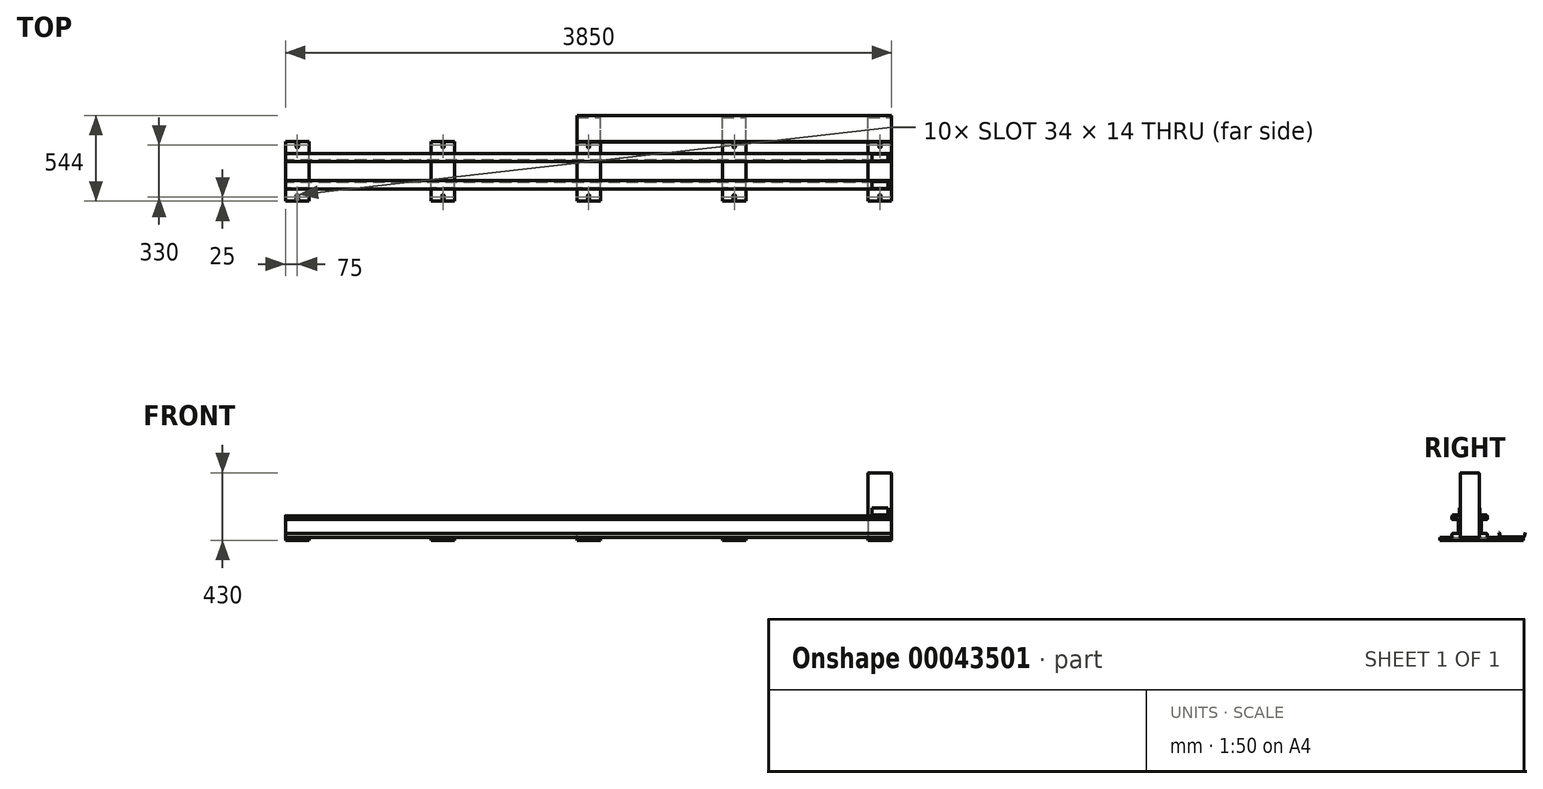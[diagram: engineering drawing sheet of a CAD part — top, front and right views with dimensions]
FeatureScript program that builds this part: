
annotation { "Feature Type Name" : "Feature", "Feature Type Description" : "" }
export const myFeature = defineFeature(function(context is Context, id is Id, definition is map)
    precondition{}
    {
        {
            var Q0;
            Q0=qCreatedBy(makeId("Top.planeOp"),FACE);
            var sketch = newSketch(context, id + "F0", { "sketchPlane" : qUnion([Q0])});
            skLineSegment(sketch, "E0.rect.bottom", {"start": v(-1925, 190) * mm, "end": v(1925, 190) * mm, "construction": true});
            skLineSegment(sketch, "E0.rect.top", {"start": v(-1925, -190) * mm, "end": v(1925, -190) * mm, "construction": true});
            skLineSegment(sketch, "E0.rect.left", {"start": v(-1925, 190) * mm, "end": v(-1925, -190) * mm, "construction": true});
            skLineSegment(sketch, "E0.rect.right", {"start": v(1925, 190) * mm, "end": v(1925, -190) * mm, "construction": true});
            skPoint(sketch, "E0.rect.middle", {"position": v(0, 0) * mm});
            skLineSegment(sketch, "E1.bottom", {"start": v(-1925, -190) * mm, "end": v(-1775, -190) * mm});
            skLineSegment(sketch, "E1.top", {"start": v(-1925, 190) * mm, "end": v(-1775, 190) * mm});
            skLineSegment(sketch, "E1.left", {"start": v(-1925, -190) * mm, "end": v(-1925, 190) * mm});
            skLineSegment(sketch, "E1.right", {"start": v(-1775, -190) * mm, "end": v(-1775, 190) * mm});
            skLineSegment(sketch, "E2", {"start": v(-1607.82, 0) * mm, "end": v(-2050.24, 0) * mm, "construction": true});
            skPoint(sketch, "E2.startSnap0", {"position": v(-1775, 0) * mm});
            skPoint(sketch, "E2.endSnap0", {"position": v(-1775, 0) * mm});
            skLineSegment(sketch, "E3", {"start": v(-1850, 190) * mm, "end": v(-1850, -266.2) * mm, "construction": true});
            skPoint(sketch, "E3.endSnap0", {"position": v(-1850, -190) * mm});
            skLineSegment(sketch, "E4.0", {"start": v(-1607.82, 155) * mm, "end": v(-2050.24, 155) * mm, "construction": true});
            skLineSegment(sketch, "E5.0", {"start": v(-1607.82, 175) * mm, "end": v(-2050.24, 175) * mm, "construction": true});
            skLineSegment(sketch, "E6", {"start": v(-1850, 175) * mm, "end": v(-1850, 155) * mm});
            skArc(sketch, "E7.0.startCap", {"start": v(-1857, 175) * mm, "mid": v(-1850, 182) * mm, "end": v(-1843, 175) * mm});
            skArc(sketch, "E7.0.endCap", {"start": v(-1843, 155) * mm, "mid": v(-1850, 148) * mm, "end": v(-1857, 155) * mm});
            skLineSegment(sketch, "E7.0.left", {"start": v(-1843, 175) * mm, "end": v(-1843, 155) * mm});
            skLineSegment(sketch, "E7.0.right", {"start": v(-1857, 175) * mm, "end": v(-1857, 155) * mm});
            skLineSegment(sketch, "E8.MirrorCS", {"start": v(-1857, -175) * mm, "end": v(-1857, -155) * mm});
            skLineSegment(sketch, "E9.MirrorCS", {"start": v(-1850, -175) * mm, "end": v(-1850, -155) * mm});
            skArc(sketch, "E10.MirrorCS", {"start": v(-1857, -175) * mm, "mid": v(-1850, -182) * mm, "end": v(-1843, -175) * mm});
            skArc(sketch, "E11.MirrorCS", {"start": v(-1843, -155) * mm, "mid": v(-1850, -148) * mm, "end": v(-1857, -155) * mm});
            skLineSegment(sketch, "E12.MirrorCS", {"start": v(-1843, -175) * mm, "end": v(-1843, -155) * mm});
            skLineSegment(sketch, "E13.1.0.0", {"start": v(-1000, -190) * mm, "end": v(-850, -190) * mm});
            skLineSegment(sketch, "E13.1.0.1", {"start": v(-1000, 190) * mm, "end": v(-850, 190) * mm});
            skPoint(sketch, "E13.1.0.2", {"position": v(-850, 0) * mm});
            skLineSegment(sketch, "E13.1.0.3", {"start": v(-1000, -190) * mm, "end": v(-1000, 190) * mm});
            skLineSegment(sketch, "E13.1.0.4", {"start": v(-850, -190) * mm, "end": v(-850, 190) * mm});
            skPoint(sketch, "E13.1.0.5", {"position": v(-925, -190) * mm});
            skLineSegment(sketch, "E13.1.0.6", {"start": v(-1000, 190) * mm, "end": v(-1000, -190) * mm, "construction": true});
            skPoint(sketch, "E13.1.0.7", {"position": v(-850, 0) * mm});
            skLineSegment(sketch, "E13.1.0.8", {"start": v(-932, -175) * mm, "end": v(-932, -155) * mm});
            skArc(sketch, "E13.1.0.9", {"start": v(-932, 175) * mm, "mid": v(-925, 182) * mm, "end": v(-918, 175) * mm});
            skArc(sketch, "E13.1.0.10", {"start": v(-932, -175) * mm, "mid": v(-925, -182) * mm, "end": v(-918, -175) * mm});
            skArc(sketch, "E13.1.0.11", {"start": v(-918, 155) * mm, "mid": v(-925, 148) * mm, "end": v(-932, 155) * mm});
            skLineSegment(sketch, "E13.1.0.12", {"start": v(-918, 175) * mm, "end": v(-918, 155) * mm});
            skLineSegment(sketch, "E13.1.0.13", {"start": v(-918, -175) * mm, "end": v(-918, -155) * mm});
            skLineSegment(sketch, "E13.1.0.14", {"start": v(-925, 175) * mm, "end": v(-925, 155) * mm});
            skLineSegment(sketch, "E13.1.0.15", {"start": v(-925, -175) * mm, "end": v(-925, -155) * mm});
            skLineSegment(sketch, "E13.1.0.16", {"start": v(-932, 175) * mm, "end": v(-932, 155) * mm});
            skArc(sketch, "E13.1.0.17", {"start": v(-918, -155) * mm, "mid": v(-925, -148) * mm, "end": v(-932, -155) * mm});
            skLineSegment(sketch, "E13.2.0.0", {"start": v(-75, -190) * mm, "end": v(75, -190) * mm});
            skPoint(sketch, "E13.2.0.2", {"position": v(75, 0) * mm});
            skLineSegment(sketch, "E13.2.0.3", {"start": v(-75, -190) * mm, "end": v(-75, 190) * mm});
            skLineSegment(sketch, "E13.2.0.4", {"start": v(75, -190) * mm, "end": v(75, 190) * mm});
            skPoint(sketch, "E13.2.0.5", {"position": v(0, -190) * mm});
            skLineSegment(sketch, "E13.2.0.6", {"start": v(-75, 190) * mm, "end": v(-75, -190) * mm, "construction": true});
            skPoint(sketch, "E13.2.0.7", {"position": v(75, 0) * mm});
            skLineSegment(sketch, "E13.2.0.8", {"start": v(-7, -175) * mm, "end": v(-7, -155) * mm});
            skArc(sketch, "E13.2.0.9", {"start": v(-7, 175) * mm, "mid": v(0, 182) * mm, "end": v(7, 175) * mm});
            skArc(sketch, "E13.2.0.10", {"start": v(-7, -175) * mm, "mid": v(0, -182) * mm, "end": v(7, -175) * mm});
            skArc(sketch, "E13.2.0.11", {"start": v(7, 155) * mm, "mid": v(0, 148) * mm, "end": v(-7, 155) * mm});
            skLineSegment(sketch, "E13.2.0.12", {"start": v(7, 175) * mm, "end": v(7, 155) * mm});
            skLineSegment(sketch, "E13.2.0.13", {"start": v(7, -175) * mm, "end": v(7, -155) * mm});
            skLineSegment(sketch, "E13.2.0.14", {"start": v(0, 175) * mm, "end": v(0, 155) * mm});
            skLineSegment(sketch, "E13.2.0.15", {"start": v(0, -175) * mm, "end": v(0, -155) * mm});
            skLineSegment(sketch, "E13.2.0.16", {"start": v(-7, 175) * mm, "end": v(-7, 155) * mm});
            skArc(sketch, "E13.2.0.17", {"start": v(7, -155) * mm, "mid": v(0, -148) * mm, "end": v(-7, -155) * mm});
            skLineSegment(sketch, "E13.3.0.0", {"start": v(850, -190) * mm, "end": v(1000, -190) * mm});
            skPoint(sketch, "E13.3.0.2", {"position": v(1000, 0) * mm});
            skLineSegment(sketch, "E13.3.0.3", {"start": v(850, -190) * mm, "end": v(850, 190) * mm});
            skLineSegment(sketch, "E13.3.0.4", {"start": v(1000, -190) * mm, "end": v(1000, 190) * mm});
            skPoint(sketch, "E13.3.0.5", {"position": v(925, -190) * mm});
            skLineSegment(sketch, "E13.3.0.6", {"start": v(850, 190) * mm, "end": v(850, -190) * mm, "construction": true});
            skPoint(sketch, "E13.3.0.7", {"position": v(1000, 0) * mm});
            skLineSegment(sketch, "E13.3.0.8", {"start": v(918, -175) * mm, "end": v(918, -155) * mm});
            skArc(sketch, "E13.3.0.9", {"start": v(918, 175) * mm, "mid": v(925, 182) * mm, "end": v(932, 175) * mm});
            skArc(sketch, "E13.3.0.10", {"start": v(918, -175) * mm, "mid": v(925, -182) * mm, "end": v(932, -175) * mm});
            skArc(sketch, "E13.3.0.11", {"start": v(932, 155) * mm, "mid": v(925, 148) * mm, "end": v(918, 155) * mm});
            skLineSegment(sketch, "E13.3.0.12", {"start": v(932, 175) * mm, "end": v(932, 155) * mm});
            skLineSegment(sketch, "E13.3.0.13", {"start": v(932, -175) * mm, "end": v(932, -155) * mm});
            skLineSegment(sketch, "E13.3.0.14", {"start": v(925, 175) * mm, "end": v(925, 155) * mm});
            skLineSegment(sketch, "E13.3.0.15", {"start": v(925, -175) * mm, "end": v(925, -155) * mm});
            skLineSegment(sketch, "E13.3.0.16", {"start": v(918, 175) * mm, "end": v(918, 155) * mm});
            skArc(sketch, "E13.3.0.17", {"start": v(932, -155) * mm, "mid": v(925, -148) * mm, "end": v(918, -155) * mm});
            skLineSegment(sketch, "E13.4.0.0", {"start": v(1775, -190) * mm, "end": v(1925, -190) * mm});
            skPoint(sketch, "E13.4.0.2", {"position": v(1925, 0) * mm});
            skLineSegment(sketch, "E13.4.0.3", {"start": v(1775, -190) * mm, "end": v(1775, 190) * mm});
            skLineSegment(sketch, "E13.4.0.4", {"start": v(1925, -190) * mm, "end": v(1925, 190) * mm});
            skPoint(sketch, "E13.4.0.5", {"position": v(1850, -190) * mm});
            skLineSegment(sketch, "E13.4.0.6", {"start": v(1775, 190) * mm, "end": v(1775, -190) * mm, "construction": true});
            skPoint(sketch, "E13.4.0.7", {"position": v(1925, 0) * mm});
            skLineSegment(sketch, "E13.4.0.8", {"start": v(1843, -175) * mm, "end": v(1843, -155) * mm});
            skArc(sketch, "E13.4.0.9", {"start": v(1843, 175) * mm, "mid": v(1850, 182) * mm, "end": v(1857, 175) * mm});
            skArc(sketch, "E13.4.0.10", {"start": v(1843, -175) * mm, "mid": v(1850, -182) * mm, "end": v(1857, -175) * mm});
            skArc(sketch, "E13.4.0.11", {"start": v(1857, 155) * mm, "mid": v(1850, 148) * mm, "end": v(1843, 155) * mm});
            skLineSegment(sketch, "E13.4.0.12", {"start": v(1857, 175) * mm, "end": v(1857, 155) * mm});
            skLineSegment(sketch, "E13.4.0.13", {"start": v(1857, -175) * mm, "end": v(1857, -155) * mm});
            skLineSegment(sketch, "E13.4.0.14", {"start": v(1850, 175) * mm, "end": v(1850, 155) * mm});
            skLineSegment(sketch, "E13.4.0.15", {"start": v(1850, -175) * mm, "end": v(1850, -155) * mm});
            skLineSegment(sketch, "E13.4.0.16", {"start": v(1843, 175) * mm, "end": v(1843, 155) * mm});
            skArc(sketch, "E13.4.0.17", {"start": v(1857, -155) * mm, "mid": v(1850, -148) * mm, "end": v(1843, -155) * mm});
            skLineSegment(sketch, "E13.direction1", {"start": v(-1925, -190) * mm, "end": v(-1000, -190) * mm, "construction": true});
            skLineSegment(sketch, "E14.top", {"start": v(-75, 340) * mm, "end": v(75, 340) * mm});
            skLineSegment(sketch, "E14.left", {"start": v(-75, -190) * mm, "end": v(-75, 340) * mm});
            skLineSegment(sketch, "E14.right", {"start": v(75, -190) * mm, "end": v(75, 340) * mm});
            skLineSegment(sketch, "E15.1.0.0", {"start": v(850, 340) * mm, "end": v(1000, 340) * mm});
            skLineSegment(sketch, "E15.1.0.1", {"start": v(1000, -190) * mm, "end": v(1000, 340) * mm});
            skLineSegment(sketch, "E15.1.0.2", {"start": v(850, -190) * mm, "end": v(850, 340) * mm});
            skLineSegment(sketch, "E15.2.0.0", {"start": v(1775, 340) * mm, "end": v(1925, 340) * mm});
            skLineSegment(sketch, "E15.2.0.1", {"start": v(1925, -190) * mm, "end": v(1925, 340) * mm});
            skLineSegment(sketch, "E15.2.0.2", {"start": v(1775, -190) * mm, "end": v(1775, 340) * mm});
            skLineSegment(sketch, "E15.direction1", {"start": v(-75, 340) * mm, "end": v(850, 340) * mm, "construction": true});
            skSolve(sketch);
        }
        {
            var Q0;
            Q0=qSketchRegion(id+"F0",true);
            extrude(context, id + "F1", {"entities" : qUnion([Q0]), "oppositeDirection" : true, "depth" : 20 * mm});
        }
        {
            var Q0;
            Q0=qCreatedBy(makeId("Right.planeOp"),FACE);
            var sketch = newSketch(context, id + "F2", { "sketchPlane" : qUnion([Q0])});
            skLineSegment(sketch, "E16", {"start": v(0, 0) * mm, "end": v(0, 313.62) * mm, "construction": true});
            skLineSegment(sketch, "E17.0", {"start": v(-113, 0) * mm, "end": v(-113, 313.62) * mm, "construction": true});
            skLineSegment(sketch, "E18.bottom", {"start": v(-108, 0) * mm, "end": v(-65, 0) * mm});
            skLineSegment(sketch, "E18.top", {"start": v(-108, 135.5) * mm, "end": v(-65, 135.5) * mm});
            skLineSegment(sketch, "E18.left", {"start": v(-113, 5) * mm, "end": v(-113, 18) * mm});
            skLineSegment(sketch, "E18.right", {"start": v(-60, 5) * mm, "end": v(-60, 130.5) * mm});
            skLineSegment(sketch, "E19.rect.bottom", {"start": v(-108, 112.5) * mm, "end": v(-77.5, 112.5) * mm});
            skLineSegment(sketch, "E19.rect.top", {"start": v(-108, 23) * mm, "end": v(-77.5, 23) * mm});
            skLineSegment(sketch, "E19.rect.right", {"start": v(-72.5, 107.5) * mm, "end": v(-72.5, 28) * mm});
            skPoint(sketch, "E19.rect.middle", {"position": v(-113, 67.75) * mm});
            skPoint(sketch, "E19.rect.left.start.orphan", {"position": v(-153.5, 112.5) * mm});
            skPoint(sketch, "E20.orphan", {"position": v(-153.5, 23) * mm});
            skLineSegment(sketch, "E21.trimOffspring", {"start": v(-113, 117.5) * mm, "end": v(-113, 130.5) * mm});
            skPoint(sketch, "E22.visualSharp", {"position": v(-113, 135.5) * mm});
            skArc(sketch, "E22.filletArc", {"start": v(-108, 135.5) * mm, "mid": v(-111.54, 134.04) * mm, "end": v(-113, 130.5) * mm});
            skPoint(sketch, "E23.visualSharp", {"position": v(-113, 0) * mm});
            skArc(sketch, "E23.filletArc", {"start": v(-113, 5) * mm, "mid": v(-111.54, 1.46) * mm, "end": v(-108, 0) * mm});
            skPoint(sketch, "E24.visualSharp", {"position": v(-60, 135.5) * mm});
            skArc(sketch, "E24.filletArc", {"start": v(-60, 130.5) * mm, "mid": v(-61.46, 134.04) * mm, "end": v(-65, 135.5) * mm});
            skPoint(sketch, "E25.visualSharp", {"position": v(-60, 0) * mm});
            skArc(sketch, "E25.filletArc", {"start": v(-65, 0) * mm, "mid": v(-61.46, 1.46) * mm, "end": v(-60, 5) * mm});
            skPoint(sketch, "E26.visualSharp", {"position": v(-72.5, 23) * mm});
            skArc(sketch, "E26.filletArc", {"start": v(-77.5, 23) * mm, "mid": v(-73.96, 24.46) * mm, "end": v(-72.5, 28) * mm});
            skPoint(sketch, "E27.visualSharp", {"position": v(-72.5, 112.5) * mm});
            skArc(sketch, "E27.filletArc", {"start": v(-72.5, 107.5) * mm, "mid": v(-73.96, 111.04) * mm, "end": v(-77.5, 112.5) * mm});
            skPoint(sketch, "E28.visualSharp", {"position": v(-113, 112.5) * mm});
            skArc(sketch, "E28.filletArc", {"start": v(-113, 117.5) * mm, "mid": v(-111.54, 113.96) * mm, "end": v(-108, 112.5) * mm});
            skPoint(sketch, "E29.visualSharp", {"position": v(-113, 23) * mm});
            skArc(sketch, "E29.filletArc", {"start": v(-108, 23) * mm, "mid": v(-111.54, 21.54) * mm, "end": v(-113, 18) * mm});
            skArc(sketch, "E30.MirrorCS", {"start": v(60, 130.5) * mm, "mid": v(61.46, 134.04) * mm, "end": v(65, 135.5) * mm});
            skLineSegment(sketch, "E31.MirrorCS", {"start": v(113, 5) * mm, "end": v(113, 18) * mm});
            skLineSegment(sketch, "E32.MirrorCS", {"start": v(113, 117.5) * mm, "end": v(113, 130.5) * mm});
            skArc(sketch, "E33.MirrorCS", {"start": v(108, 135.5) * mm, "mid": v(111.54, 134.04) * mm, "end": v(113, 130.5) * mm});
            skArc(sketch, "E34.MirrorCS", {"start": v(113, 5) * mm, "mid": v(111.54, 1.46) * mm, "end": v(108, 0) * mm});
            skArc(sketch, "E35.MirrorCS", {"start": v(72.5, 107.5) * mm, "mid": v(73.96, 111.04) * mm, "end": v(77.5, 112.5) * mm});
            skArc(sketch, "E36.MirrorCS", {"start": v(77.5, 23) * mm, "mid": v(73.96, 24.46) * mm, "end": v(72.5, 28) * mm});
            skArc(sketch, "E37.MirrorCS", {"start": v(65, 0) * mm, "mid": v(61.46, 1.46) * mm, "end": v(60, 5) * mm});
            skArc(sketch, "E38.MirrorCS", {"start": v(113, 117.5) * mm, "mid": v(111.54, 113.96) * mm, "end": v(108, 112.5) * mm});
            skArc(sketch, "E39.MirrorCS", {"start": v(108, 23) * mm, "mid": v(111.54, 21.54) * mm, "end": v(113, 18) * mm});
            skPoint(sketch, "E40.MirrorP", {"position": v(60, 135.5) * mm});
            skLineSegment(sketch, "E41.MirrorCS", {"start": v(108, 112.5) * mm, "end": v(77.5, 112.5) * mm});
            skLineSegment(sketch, "E42.MirrorCS", {"start": v(60, 5) * mm, "end": v(60, 130.5) * mm});
            skLineSegment(sketch, "E43.MirrorCS", {"start": v(108, 23) * mm, "end": v(77.5, 23) * mm});
            skLineSegment(sketch, "E44.MirrorCS", {"start": v(72.5, 107.5) * mm, "end": v(72.5, 28) * mm});
            skLineSegment(sketch, "E45.MirrorCS", {"start": v(108, 135.5) * mm, "end": v(65, 135.5) * mm});
            skLineSegment(sketch, "E46.MirrorCS", {"start": v(108, 0) * mm, "end": v(65, 0) * mm});
            skPoint(sketch, "E47.MirrorP", {"position": v(113, 67.75) * mm});
            skPoint(sketch, "E48.MirrorP", {"position": v(113, 0) * mm});
            skPoint(sketch, "E49.MirrorP", {"position": v(72.5, 23) * mm});
            skPoint(sketch, "E50.MirrorP", {"position": v(72.5, 112.5) * mm});
            skPoint(sketch, "E51.MirrorP", {"position": v(113, 135.5) * mm});
            skPoint(sketch, "E52.MirrorP", {"position": v(60, 0) * mm});
            skPoint(sketch, "E53.MirrorP", {"position": v(113, 23) * mm});
            skPoint(sketch, "E54.MirrorP", {"position": v(113, 112.5) * mm});
            skSolve(sketch);
        }
        {
            var Q0;
            Q0=qSketchRegion(id+"F2",true);
            extrude(context, id + "F3", {"entities" : qUnion([Q0]), "operationType" : NewBodyOperationType.ADD, "endBound" : BoundingType.SYMMETRIC, "depth" : 3850 * mm});
        }
        {
            var Q0;
            Q0=makeQuery(id+"F1.opExtrude","SWEPT_FACE",FACE,{"disambiguationData":[OSD([sQuery(id+"F0.wireOp",EDGE,"E15.2.0.1")])]});
            var sketch = newSketch(context, id + "F4", { "sketchPlane" : qUnion([Q0])});
            skLineSegment(sketch, "E55.0", {"start": v(-190, -20) * mm, "end": v(-190, 0) * mm, "construction": true});
            skLineSegment(sketch, "E56.0", {"start": v(354, -20) * mm, "end": v(354, 30) * mm, "construction": true});
            skLineSegment(sketch, "E57.0", {"start": v(346.5, -20) * mm, "end": v(346.5, 0) * mm, "construction": true});
            skLineSegment(sketch, "E58.0", {"start": v(269.5, -20) * mm, "end": v(269.5, 0) * mm, "construction": true});
            skLineSegment(sketch, "E59", {"start": v(354, 30) * mm, "end": v(347.83, 5.3) * mm});
            skLineSegment(sketch, "E60", {"start": v(341.03, 0) * mm, "end": v(269.5, 0) * mm});
            skLineSegment(sketch, "E61.0", {"start": v(341.03, 2) * mm, "end": v(269.5, 2) * mm});
            skLineSegment(sketch, "E61.1", {"start": v(352.06, 30.49) * mm, "end": v(345.89, 5.79) * mm});
            skLineSegment(sketch, "E62", {"start": v(352.06, 30.49) * mm, "end": v(354, 30) * mm});
            skLineSegment(sketch, "E63.MirrorCS", {"start": v(197.97, 0) * mm, "end": v(269.5, 0) * mm});
            skLineSegment(sketch, "E64.MirrorCS", {"start": v(197.97, 2) * mm, "end": v(269.5, 2) * mm});
            skLineSegment(sketch, "E65.MirrorCS", {"start": v(186.94, 30.49) * mm, "end": v(193.11, 5.79) * mm});
            skLineSegment(sketch, "E66.MirrorCS", {"start": v(185, 30) * mm, "end": v(191.17, 5.3) * mm});
            skLineSegment(sketch, "E67.MirrorCS", {"start": v(186.94, 30.49) * mm, "end": v(185, 30) * mm});
            skPoint(sketch, "E68.visualSharp", {"position": v(344.94, 2) * mm});
            skArc(sketch, "E68.filletArc", {"start": v(341.03, 2) * mm, "mid": v(344.11, 3.06) * mm, "end": v(345.89, 5.79) * mm});
            skPoint(sketch, "E69.visualSharp", {"position": v(194.06, 2) * mm});
            skArc(sketch, "E69.filletArc", {"start": v(193.11, 5.79) * mm, "mid": v(194.89, 3.06) * mm, "end": v(197.97, 2) * mm});
            skPoint(sketch, "E70.visualSharp", {"position": v(346.5, 0) * mm});
            skArc(sketch, "E70.filletArc", {"start": v(341.03, 0) * mm, "mid": v(345.34, 1.48) * mm, "end": v(347.83, 5.3) * mm});
            skPoint(sketch, "E71.visualSharp", {"position": v(192.5, 0) * mm});
            skArc(sketch, "E71.filletArc", {"start": v(191.17, 5.3) * mm, "mid": v(193.66, 1.48) * mm, "end": v(197.97, 0) * mm});
            skSolve(sketch);
        }
        {
            var Q0;
            Q0=qSketchRegion(id+"F4",true);
            var Q1;
            Q1=makeQuery(id+"F1.opExtrude","SWEPT_FACE",FACE,{"disambiguationData":[OSD([sQuery(id+"F0.wireOp",EDGE,"E14.left")])]});
            extrude(context, id + "F5", {"entities" : qUnion([Q0]), "endBound" : BoundingType.UP_TO_SURFACE, "oppositeDirection" : true, "endBoundEntityFace" : qUnion([Q1]), "depth" : 25 * mm});
        }
        {
            var Q0;
            Q0=makeQuery(id+"F1.opExtrude","CAP_FACE",FACE,{"disambiguationData":[OSD([sQuery(id+"F0.wireOp",EDGE,"E13.4.0.0"),sQuery(id+"F0.wireOp",EDGE,"E13.4.0.8"),sQuery(id+"F0.wireOp",EDGE,"E13.4.0.9"),sQuery(id+"F0.wireOp",EDGE,"E13.4.0.10"),sQuery(id+"F0.wireOp",EDGE,"E13.4.0.11"),sQuery(id+"F0.wireOp",EDGE,"E13.4.0.12"),sQuery(id+"F0.wireOp",EDGE,"E13.4.0.13"),sQuery(id+"F0.wireOp",EDGE,"E13.4.0.16"),sQuery(id+"F0.wireOp",EDGE,"E13.4.0.17"),sQuery(id+"F0.wireOp",EDGE,"E15.2.0.0"),sQuery(id+"F0.wireOp",EDGE,"E15.2.0.1"),sQuery(id+"F0.wireOp",EDGE,"E15.2.0.2")])],"isStart":true});
            var sketch = newSketch(context, id + "F6", { "sketchPlane" : qUnion([Q0])});
            skLineSegment(sketch, "E72.0", {"start": v(1925, 60) * mm, "end": v(-1925, 60) * mm});
            skLineSegment(sketch, "E73.0", {"start": v(1925, -60) * mm, "end": v(-1925, -60) * mm});
            skLineSegment(sketch, "E74.0", {"start": v(1925, -190) * mm, "end": v(1925, 340) * mm});
            skLineSegment(sketch, "E75.0", {"start": v(1775, -190) * mm, "end": v(1775, 340) * mm});
            skSolve(sketch);
        }
        {
            var Q0;
            Q0=qSketchRegion(id+"F6",true);
            extrude(context, id + "F7", {"entities" : qUnion([Q0]), "depth" : 410 * mm});
        }
        {
            var Q0;
            Q0=makeQuery(id+"F7.opExtrude","SWEPT_EDGE",EDGE,{"disambiguationData":[OSD([sQuery(id+"F6.wireOp",EDGE,"E73.0"),sQuery(id+"F6.wireOp",EDGE,"E74.0")])]});
            var Q1;
            Q1=makeQuery(id+"F7.opExtrude","SWEPT_EDGE",EDGE,{"disambiguationData":[OSD([sQuery(id+"F6.wireOp",EDGE,"E73.0"),sQuery(id+"F6.wireOp",EDGE,"E75.0")])]});
            var Q2;
            Q2=makeQuery(id+"F7.opExtrude","SWEPT_EDGE",EDGE,{"disambiguationData":[OSD([sQuery(id+"F6.wireOp",EDGE,"E72.0"),sQuery(id+"F6.wireOp",EDGE,"E74.0")])]});
            var Q3;
            Q3=makeQuery(id+"F7.opExtrude","SWEPT_EDGE",EDGE,{"disambiguationData":[OSD([sQuery(id+"F6.wireOp",EDGE,"E72.0"),sQuery(id+"F6.wireOp",EDGE,"E75.0")])]});
            var Q4;
            Q4=makeQuery(id+"F7.opExtrude","CAP_FACE",FACE,{"disambiguationData":[OSD([sQuery(id+"F6.wireOp",EDGE,"E72.0"),sQuery(id+"F6.wireOp",EDGE,"E73.0"),sQuery(id+"F6.wireOp",EDGE,"E74.0"),sQuery(id+"F6.wireOp",EDGE,"E75.0")])],"isStart":false});
            fillet(context, id + "F8", {"entities" : qUnion([Q0, Q1, Q2, Q3, Q4]), "radius" : 5 * mm, "tangentPropagation" : true, "allowEdgeOverflow" : false});
        }
        {
            var Q0;
            Q0=makeQuery(id+"F7.opExtrude","SWEPT_FACE",FACE,{"disambiguationData":[OSD([sQuery(id+"F6.wireOp",EDGE,"E74.0")])]});
            fillet(context, id + "F9", {"entities" : qUnion([Q0]), "radius" : 5 * mm, "tangentPropagation" : true, "allowEdgeOverflow" : false});
        }
        {
            var Q0;
            Q0=makeQuery(id+"F7.opExtrude","SWEPT_FACE",FACE,{"disambiguationData":[OSD([sQuery(id+"F6.wireOp",EDGE,"E74.0")])]});
            cPlane(context, id + "F10", {"entities" : qUnion([Q0]), "cplaneType" : CPlaneType.OFFSET, "offset" : 75 * mm, "oppositeDirection" : true, "width" : 150 * mm, "height" : 150 * mm});
        }
        {
            var Q0;
            Q0=qCreatedBy(id+"F10.planeOp",FACE);
            var sketch = newSketch(context, id + "F11", { "sketchPlane" : qUnion([Q0])});
            skLineSegment(sketch, "E76.0", {"start": v(-60, 5) * mm, "end": v(-60, 405) * mm});
            skLineSegment(sketch, "E77.0", {"start": v(-108, 135.5) * mm, "end": v(-63.62, 135.5) * mm});
            skPoint(sketch, "E78.orphan", {"position": v(-65, 135.5) * mm});
            skLineSegment(sketch, "E79.bottom", {"start": v(-60, 135.5) * mm, "end": v(-110, 135.5) * mm});
            skLineSegment(sketch, "E79.top", {"start": v(-60, 185.5) * mm, "end": v(-65, 185.5) * mm});
            skLineSegment(sketch, "E79.left", {"start": v(-60, 135.5) * mm, "end": v(-60, 185.5) * mm});
            skLineSegment(sketch, "E79.right", {"start": v(-110, 135.5) * mm, "end": v(-110, 185.5) * mm});
            skLineSegment(sketch, "E80.top", {"start": v(-110, 140.5) * mm, "end": v(-70, 140.5) * mm});
            skLineSegment(sketch, "E80.right", {"start": v(-65, 185.5) * mm, "end": v(-65, 145.5) * mm});
            skPoint(sketch, "E81.visualSharp", {"position": v(-65, 140.5) * mm});
            skArc(sketch, "E81.filletArc", {"start": v(-70, 140.5) * mm, "mid": v(-66.46, 141.96) * mm, "end": v(-65, 145.5) * mm});
            skSolve(sketch);
        }
        {
            var Q0;
            Q0=qSketchRegion(id+"F11",true);
            extrude(context, id + "F12", {"entities" : qUnion([Q0]), "endBound" : BoundingType.SYMMETRIC, "depth" : 100 * mm});
        }
        {
            var Q0;
            Q0=makeQuery(id+"F12.opExtrude","SWEPT_BODY",BODY,{"disambiguationData":[OSD([sQuery(id+"F11.wireOp",EDGE,"E79.bottom"),sQuery(id+"F11.wireOp",EDGE,"E79.top"),sQuery(id+"F11.wireOp",EDGE,"E79.left"),sQuery(id+"F11.wireOp",EDGE,"E79.right"),sQuery(id+"F11.wireOp",EDGE,"E80.top"),sQuery(id+"F11.wireOp",EDGE,"E80.right"),sQuery(id+"F11.wireOp",EDGE,"E81.filletArc")])]});
            var Q1;
            Q1=qCreatedBy(makeId("Front.planeOp"),FACE);
            mirror(context, id + "F13", {"entities" : qUnion([Q0]), "mirrorPlane" : qUnion([Q1])});
        }
    });
